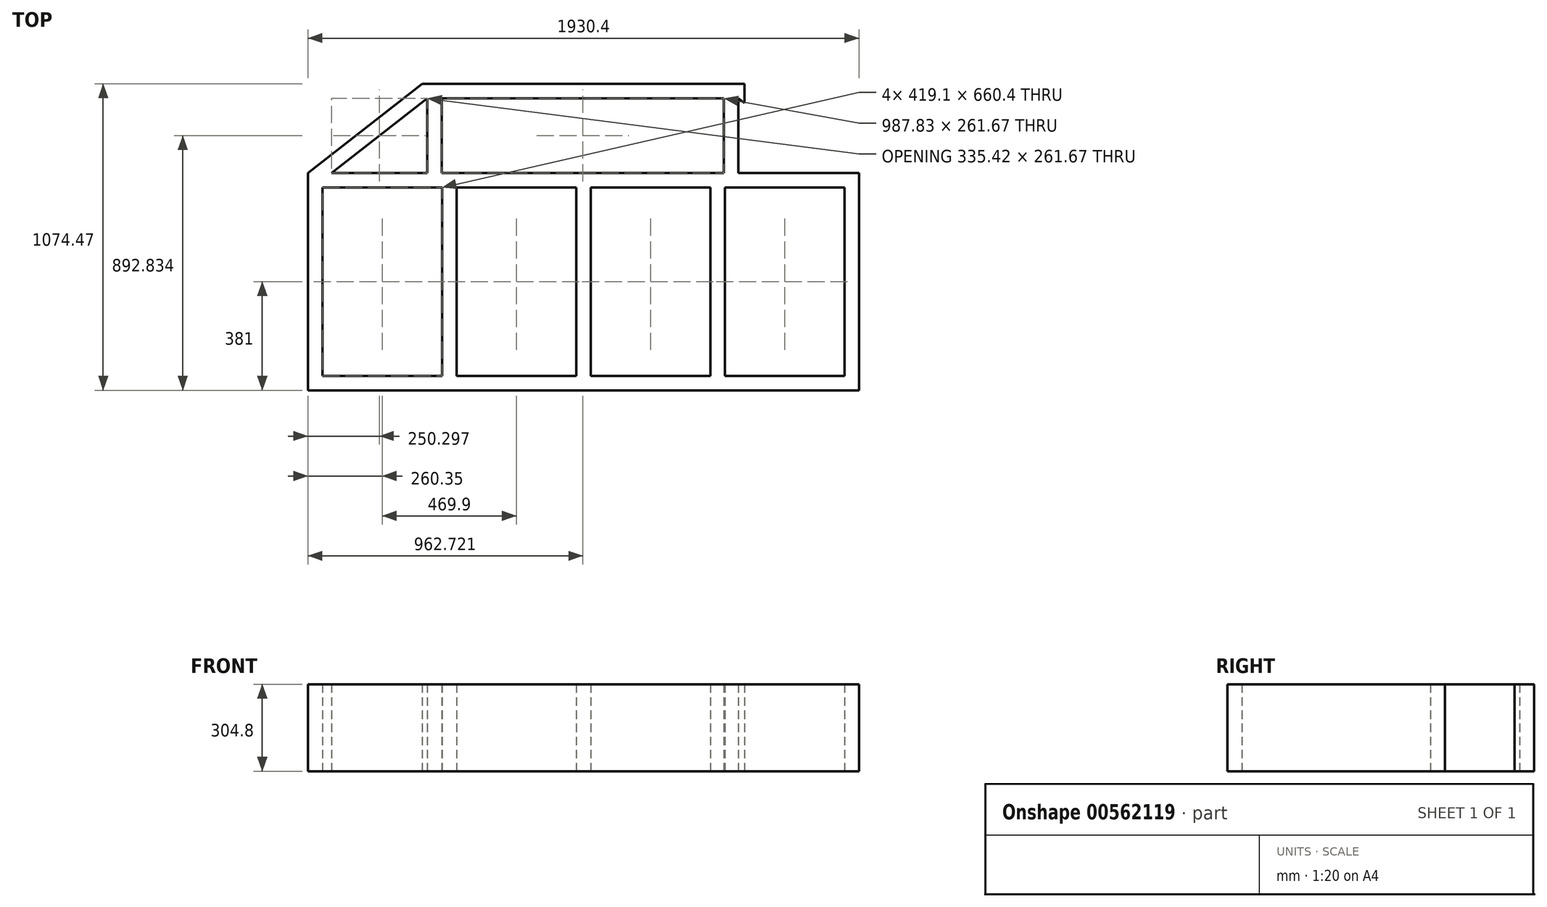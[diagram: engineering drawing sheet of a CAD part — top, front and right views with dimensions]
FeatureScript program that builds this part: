
annotation { "Feature Type Name" : "Feature", "Feature Type Description" : "" }
export const myFeature = defineFeature(function(context is Context, id is Id, definition is map)
    precondition{}
    {
        {
            var Q0;
            Q0=qCreatedBy(makeId("Top.planeOp"),FACE);
            var sketch = newSketch(context, id + "F0", { "sketchPlane" : qUnion([Q0])});
            skLineSegment(sketch, "E0.bottom", {"start": v(965.2, 381) * mm, "end": v(-965.2, 381) * mm});
            skLineSegment(sketch, "E0.top", {"start": v(965.2, -381) * mm, "end": v(-965.2, -381) * mm});
            skLineSegment(sketch, "E0.left", {"start": v(965.2, 381) * mm, "end": v(965.2, -381) * mm});
            skLineSegment(sketch, "E0.right", {"start": v(-965.2, 381) * mm, "end": v(-965.2, -381) * mm});
            skPoint(sketch, "E0.middle", {"position": v(0, 0) * mm});
            skLineSegment(sketch, "E1", {"start": v(-965.2, 381) * mm, "end": v(-564.67, 693.47) * mm});
            skLineSegment(sketch, "E2", {"start": v(-564.67, 693.47) * mm, "end": v(564.67, 693.47) * mm});
            skLineSegment(sketch, "E3", {"start": v(564.67, 693.47) * mm, "end": v(965.2, 381) * mm});
            skLineSegment(sketch, "E4.bottom", {"start": v(914.4, 330.2) * mm, "end": v(-914.4, 330.2) * mm});
            skLineSegment(sketch, "E4.top", {"start": v(914.4, -330.2) * mm, "end": v(-914.4, -330.2) * mm});
            skLineSegment(sketch, "E4.left", {"start": v(914.4, 330.2) * mm, "end": v(914.4, -330.2) * mm});
            skLineSegment(sketch, "E4.right", {"start": v(-914.4, 330.2) * mm, "end": v(-914.4, -330.2) * mm});
            skLineSegment(sketch, "E5", {"start": v(-965.2, 381) * mm, "end": v(-882.61, 381) * mm});
            skLineSegment(sketch, "E6", {"start": v(-882.61, 381) * mm, "end": v(-547.2, 642.67) * mm});
            skLineSegment(sketch, "E7", {"start": v(-547.2, 642.67) * mm, "end": v(542.24, 642.67) * mm});
            skLineSegment(sketch, "E8", {"start": v(542.24, 642.67) * mm, "end": v(882.61, 381) * mm});
            skLineSegment(sketch, "E9", {"start": v(-914.4, 330.2) * mm, "end": v(-495.3, 330.2) * mm});
            skLineSegment(sketch, "E10", {"start": v(-495.3, 330.2) * mm, "end": v(-495.3, -330.2) * mm});
            skLineSegment(sketch, "E11", {"start": v(-495.3, -330.2) * mm, "end": v(-444.5, -330.2) * mm});
            skLineSegment(sketch, "E12", {"start": v(-444.5, -330.2) * mm, "end": v(-444.5, 330.2) * mm});
            skLineSegment(sketch, "E13", {"start": v(-444.5, 330.2) * mm, "end": v(-25.4, 330.2) * mm});
            skLineSegment(sketch, "E14", {"start": v(-25.4, 330.2) * mm, "end": v(-25.4, -330.2) * mm});
            skLineSegment(sketch, "E15", {"start": v(-25.4, -330.2) * mm, "end": v(25.4, -330.2) * mm});
            skLineSegment(sketch, "E16", {"start": v(25.4, -330.2) * mm, "end": v(25.4, 330.2) * mm});
            skLineSegment(sketch, "E17", {"start": v(25.4, 330.2) * mm, "end": v(444.5, 330.2) * mm});
            skLineSegment(sketch, "E18", {"start": v(444.5, 330.2) * mm, "end": v(444.5, -330.2) * mm});
            skLineSegment(sketch, "E19", {"start": v(444.5, -330.2) * mm, "end": v(495.3, -330.2) * mm});
            skLineSegment(sketch, "E20", {"start": v(495.3, -330.2) * mm, "end": v(495.3, 330.2) * mm});
            skLineSegment(sketch, "E21", {"start": v(495.3, 330.2) * mm, "end": v(914.4, 330.2) * mm});
            skLineSegment(sketch, "E22", {"start": v(-547.2, 642.67) * mm, "end": v(-547.2, 381) * mm});
            skLineSegment(sketch, "E23", {"start": v(-547.2, 381) * mm, "end": v(-496.4, 381) * mm});
            skLineSegment(sketch, "E24", {"start": v(-496.4, 381) * mm, "end": v(-496.4, 642.67) * mm});
            skLineSegment(sketch, "E25", {"start": v(542.24, 642.67) * mm, "end": v(542.24, 381) * mm});
            skLineSegment(sketch, "E26", {"start": v(542.24, 381) * mm, "end": v(491.44, 381) * mm});
            skLineSegment(sketch, "E27", {"start": v(491.44, 381) * mm, "end": v(491.44, 642.67) * mm});
            skLineSegment(sketch, "E28", {"start": v(564.67, 693.47) * mm, "end": v(564.67, 625.43) * mm});
            skLineSegment(sketch, "E29", {"start": v(564.67, 693.47) * mm, "end": v(542.24, 664.72) * mm});
            skSolve(sketch);
        }
        {
            var Q0;
            Q0=makeQuery(id+"F0.imprint","IMPRINT",FACE,{"disambiguationData":[TD([[makeQuery(id+"F0.imprint","IMPRINT",EDGE,{"derivedFrom":sQuery(id+"F0.wireOp",EDGE,"E1")}),-1.0]])]});
            var Q1;
            {var subQ0=sQuery(id+"F0.wireOp",EDGE,"E22");Q1=makeQuery(id+"F0.imprint","IMPRINT",FACE,{"disambiguationData":[TD([[makeQuery(id+"F0.imprint","IMPRINT",EDGE,{"derivedFrom":subQ0}),1.0]])]});}
            var Q2;
            {var subQ0=sQuery(id+"F0.wireOp",EDGE,"E25");Q2=makeQuery(id+"F0.imprint","IMPRINT",FACE,{"disambiguationData":[TD([[makeQuery(id+"F0.imprint","IMPRINT",EDGE,{"derivedFrom":subQ0}),-1.0]])]});}
            var Q3;
            Q3=makeQuery(id+"F0.imprint","IMPRINT",FACE,{"disambiguationData":[TD([[makeQuery(id+"F0.imprint","IMPRINT",EDGE,{"derivedFrom":sQuery(id+"F0.wireOp",EDGE,"E0.top")}),-1.0]])]});
            var Q4;
            {var subQ2=sQuery(id+"F0.wireOp",EDGE,"E18");Q4=makeQuery(id+"F0.imprint","IMPRINT",FACE,{"disambiguationData":[TD([[makeQuery(id+"F0.imprint","IMPRINT",EDGE,{"derivedFrom":subQ2}),1.0]])]});}
            var Q5;
            {var subQ0=sQuery(id+"F0.wireOp",EDGE,"E14");Q5=makeQuery(id+"F0.imprint","IMPRINT",FACE,{"disambiguationData":[TD([[makeQuery(id+"F0.imprint","IMPRINT",EDGE,{"derivedFrom":subQ0}),1.0]])]});}
            var Q6;
            {var subQ0=sQuery(id+"F0.wireOp",EDGE,"E10");Q6=makeQuery(id+"F0.imprint","IMPRINT",FACE,{"disambiguationData":[TD([[makeQuery(id+"F0.imprint","IMPRINT",EDGE,{"derivedFrom":subQ0}),1.0]])]});}
            extrude(context, id + "F1", {"entities" : qUnion([Q0, Q1, Q2, Q3, Q4, Q5, Q6]), "depth" : 304.8 * mm, "offsetDistance" : 25.4 * mm});
        }
    });
